# Revit family: Gleitschlitten Typ A, höhe h=100mm, Ø610 bis Ø813mm, o.D
name_source: partatom
category: HLS-Bauteile
revit_build: Autodesk Revit 2018 (Build: 20190510_1515(x64)
units: mm (PartAtom-declared; Revit-internal decimal feet)

## family parameters
Arbeitsebenenbasiert = Ja
Beim Laden mit Abzugskörper schneiden = Nein
Bemaßung runder Anschluss = Durchmesser verwenden
Gemeinsam genutzt = Ja
Immer vertikal = Nein
Klassifizierung = Keine
Raumberechnungspunkt = Nein
Teiletyp = Normal

## types (3) — shared parameters
Breite Schellenband = 70 mm
Fabrikat = MEFA
Höhe Schießnaht RS = 100 mm  [stored 0.328084 ft]
Kurztext1 = Gleitschlitten A 70 x 10 mm
Mengeneinheit = St
Schalldämmeinlage = ohne Dämmung
Sicherheitsfaktor = 1.54
Stärke Schellenband = 10 mm
Verschluss = Schraube + Mutter
Verschluss-Schraube = M20
Vorgabe-Ansicht = 1219 mm
vpe = 1
zero-valued in all types: Dämmstärke

## per-type parameters (varying)
| type | A (Breite) | Abstand RS AK | Achshöhe | Achshöhe _ | Artikelnummer | Breite Unterbau | EAN | Flachmaterial | Gewicht | Gewicht pro Bauteil | Kurztext2 | L | Länge Unterbau | RS Ø610 bis Ø813 | Rohraußendurchmesser | Stärke Material | TL Platte |
| Gleitschlitten TypA, h=100mm, o.D., Ø610mm | 289 mm  [stored 0.948163 ft] | 370 mm  [stored 1.21391 ft] | 405 mm | 405 mm | 110afa0610 | 405 mm | 4250928461704 | Flachmaterial nach DIN (45 Grad und 70-8 und 70-10) : für Ø610 o.D. | 40.34 kg | 40.34 kg | 610 mm o. Dämm. fsv | 390 mm  [stored 1.27953 ft] | 390 mm | Rohrschelle 70x10, gvz, Ø610 bis 813mm, 30Grad für Gleitschlitten richtig : Rohrschellen Form A, Typ TGA, Ø 610, gvz | 610 mm  [stored 2.00131 ft] | 10 mm  [stored 0.0328084 ft] | TL-Fuß für Gleitschl.2Lo.14 für 70-10 : TL für 10-390-125 |
| Gleitschlitten TypA, h=100mm, o.D., Ø711mm | 313 mm  [stored 1.0269 ft] | 370 mm  [stored 1.21391 ft] | 456 mm | 456 mm  [stored 1.49606 ft] | 110afa0711 | 429 mm | 4250928461711 | Flachmaterial nach DIN (45 Grad und 70-8 und 70-10) : für Ø711 o.D. | 44.39 kg | 44.39 kg | 711 mm o. Dämm. fsv | 390 mm  [stored 1.27953 ft] | 390 mm | Rohrschelle 70x10, gvz, Ø610 bis 813mm, 30Grad für Gleitschlitten richtig : Rohrschellen Form A, Typ TGA, Ø 711, gvz | 711 mm  [stored 2.33268 ft] | 10 mm  [stored 0.0328084 ft] | TL-Fuß für Gleitschl.2Lo.14 für 70-10 : TL für 10-390-125 |
| Gleitschlitten TypA, h=100mm, o.D., Ø813mm | 357 mm  [stored 1.17126 ft] | 450 mm  [stored 1.47638 ft] | 507 mm | 507 mm  [stored 1.66339 ft] | 110afa0813 | 473 mm | 4250928461728 | Flachmaterial nach DIN (45 Grad und 70-8 und 70-10) : für Ø813 o.D. | 54.46 kg | 54.46 kg | 813 mm o. Dämm. fsv | 470 mm  [stored 1.54199 ft] | 470 mm | Rohrschelle 70x10, gvz, Ø610 bis 813mm, 30Grad für Gleitschlitten richtig : Rohrschellen Form A, Typ TGA, Ø 813, gvz | 813 mm | 12 mm  [stored 0.0393701 ft] | TL-Fuß für Gleitschl.2Lo.14 für 70-10 : TL für 12-470-130 |

note: [stored X ft] marks values corroborated as IEEE doubles in the binary element streams (Revit-internal decimal feet)

## geometry (parser evidence)
native form markers: Sweep x3
no freeform markers — native parametric forms only
